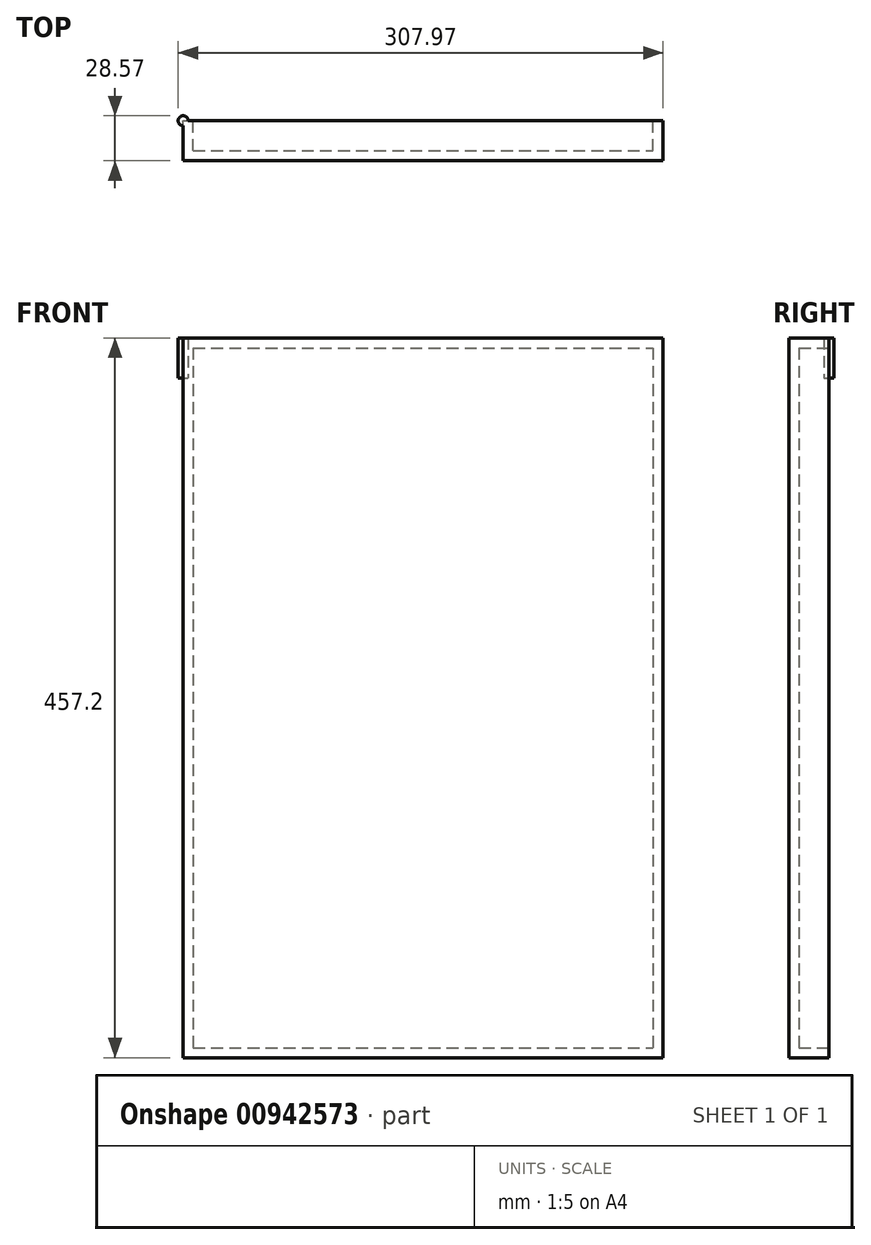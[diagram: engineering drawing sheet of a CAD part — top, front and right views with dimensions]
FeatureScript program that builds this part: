
annotation { "Feature Type Name" : "Feature", "Feature Type Description" : "" }
export const myFeature = defineFeature(function(context is Context, id is Id, definition is map)
    precondition{}
    {
        {
            var Q0;
            Q0=qCreatedBy(makeId("Front.planeOp"),FACE);
            var sketch = newSketch(context, id + "F0", { "sketchPlane" : qUnion([Q0])});
            skLineSegment(sketch, "E0.bottom", {"start": v(0, 0) * mm, "end": v(304.8, 0) * mm});
            skLineSegment(sketch, "E0.top", {"start": v(0, -457.2) * mm, "end": v(304.8, -457.2) * mm});
            skLineSegment(sketch, "E0.left", {"start": v(0, 0) * mm, "end": v(0, -457.2) * mm});
            skLineSegment(sketch, "E0.right", {"start": v(304.8, 0) * mm, "end": v(304.8, -457.2) * mm});
            skSolve(sketch);
        }
        {
            var Q0;
            Q0=sQuery(id+"F0.wireOp",EDGE,"E0.right");
            extrude(context, id + "F1", {"bodyType" : ToolBodyType.SURFACE, "surfaceEntities" : qUnion([Q0]), "depth" : 25.4 * mm, "offsetDistance" : 25.4 * mm});
        }
        {
            var Q0;
            Q0 = qSketchRegion(id + "F0", true);
            extrude(context, id + "F2", {"entities" : qUnion([Q0]), "depth" : 25.4 * mm, "offsetDistance" : 25.4 * mm});
        }
        {
            var Q0;
            Q0=makeQuery(id+"F2.opExtrude","CAP_FACE",FACE,{"disambiguationData":[OSD([sQuery(id+"F0.wireOp",EDGE,"E0.bottom"),sQuery(id+"F0.wireOp",EDGE,"E0.top"),sQuery(id+"F0.wireOp",EDGE,"E0.left"),sQuery(id+"F0.wireOp",EDGE,"E0.right")])],"isStart":true});
            shell(context, id + "F3", {"entities" : qUnion([Q0]), "thickness" : 6.35 * mm});
        }
        {
            var Q0;
            Q0=qCreatedBy(makeId("Right.planeOp"),FACE);
            var sketch = newSketch(context, id + "F4", { "sketchPlane" : qUnion([Q0])});
            skLineSegment(sketch, "E1.bottom", {"start": v(0, 0) * mm, "end": v(3.18, 0) * mm});
            skLineSegment(sketch, "E1.top", {"start": v(0, -25.4) * mm, "end": v(3.18, -25.4) * mm});
            skLineSegment(sketch, "E1.left", {"start": v(0, 0) * mm, "end": v(0, -25.4) * mm});
            skLineSegment(sketch, "E1.right", {"start": v(3.18, 0) * mm, "end": v(3.18, -25.4) * mm});
            skLineSegment(sketch, "E2", {"start": v(0, 0) * mm, "end": v(0, 79.5) * mm, "construction": true});
            skSolve(sketch);
        }
        {
            var Q0;
            Q0=makeQuery(id+"F4.imprint","IMPRINT",FACE,{"disambiguationData":[TD([[makeQuery(id+"F4.imprint","IMPRINT",EDGE,{"derivedFrom":sQuery(id+"F4.wireOp",EDGE,"E1.bottom")}),-1.0]])]});
            var Q1;
            Q1=sQuery(id+"F4.wireOp",EDGE,"E2");
            revolve(context, id + "F5", {"operationType" : NewBodyOperationType.ADD, "surfaceOperationType" : NewSurfaceOperationType.NEW, "entities" : qUnion([Q0]), "axis" : qUnion([Q1]), "revolveType" : RevolveType.FULL});
        }
    });
